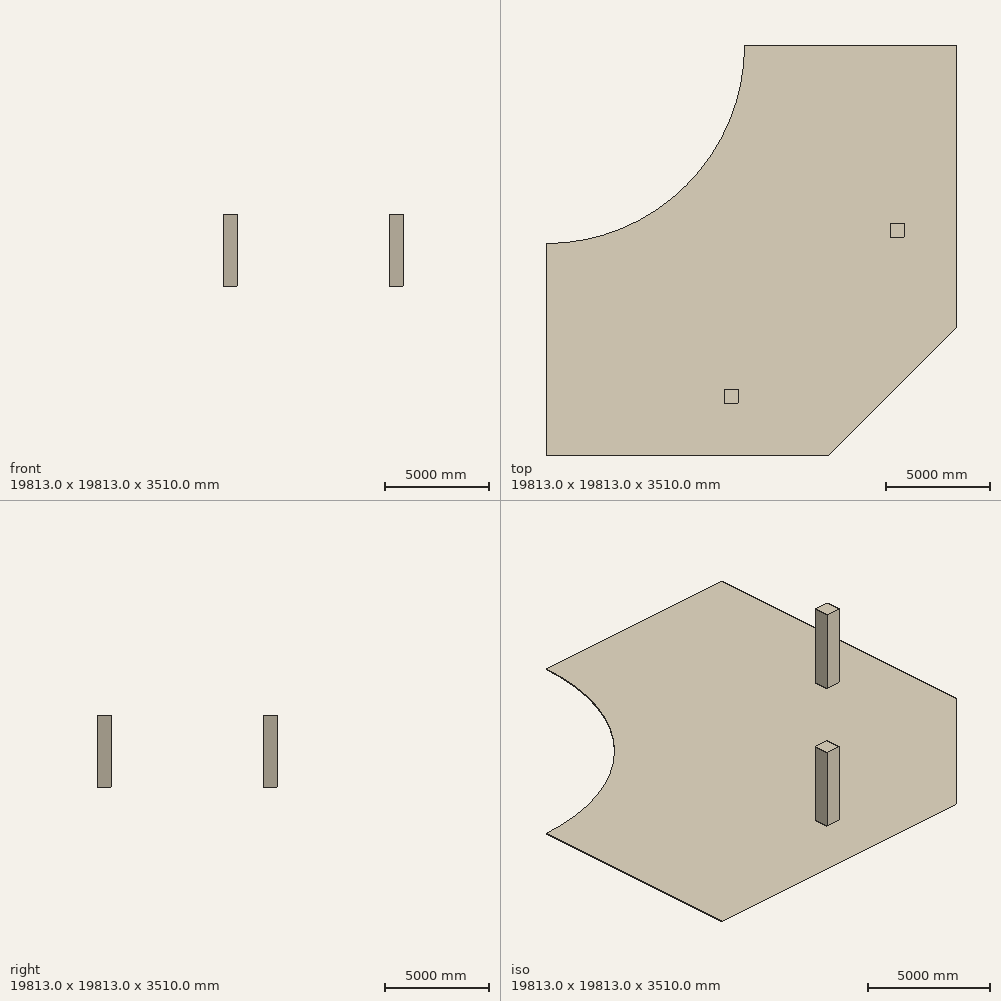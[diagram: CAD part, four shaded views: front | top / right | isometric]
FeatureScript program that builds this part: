
annotation { "Feature Type Name" : "Feature", "Feature Type Description" : "" }
export const myFeature = defineFeature(function(context is Context, id is Id, definition is map)
    precondition{}
    {
        {
            var Q0;
            Q0=qCreatedBy(makeId("Top.planeOp"),FACE);
            var sketch = newSketch(context, id + "F0", { "sketchPlane" : qUnion([Q0])});
            skLineSegment(sketch, "E0.bottom", {"start": v(0, 0) * mm, "end": v(13640, 0) * mm});
            skLineSegment(sketch, "E0.top", {"start": v(9573.04, 19813.04) * mm, "end": v(19813.04, 19813.04) * mm});
            skLineSegment(sketch, "E0.left", {"start": v(0, 0) * mm, "end": v(0, 10240) * mm});
            skLineSegment(sketch, "E0.right", {"start": v(19813.04, 6173.04) * mm, "end": v(19813.04, 19813.04) * mm});
            skLineSegment(sketch, "E1", {"start": v(13640, 0) * mm, "end": v(19813.04, 6173.04) * mm});
            skArc(sketch, "E2", {"start": v(0, 10240) * mm, "mid": v(6769.16, 13043.88) * mm, "end": v(9573.04, 19813.04) * mm});
            skLineSegment(sketch, "E3", {"start": v(19813.04, 10240) * mm, "end": v(0, 10240) * mm, "construction": true});
            skLineSegment(sketch, "E4", {"start": v(9573.04, 19813.04) * mm, "end": v(9573.04, 0) * mm, "construction": true});
            skLineSegment(sketch, "E5.bottom", {"start": v(16613.04, 11213.04) * mm, "end": v(17313.04, 11213.04) * mm});
            skLineSegment(sketch, "E5.top", {"start": v(16613.04, 10513.04) * mm, "end": v(17313.04, 10513.04) * mm});
            skLineSegment(sketch, "E5.left", {"start": v(16613.04, 11213.04) * mm, "end": v(16613.04, 10513.04) * mm});
            skLineSegment(sketch, "E5.right", {"start": v(17313.04, 11213.04) * mm, "end": v(17313.04, 10513.04) * mm});
            skLineSegment(sketch, "E6.bottom", {"start": v(8600, 3200) * mm, "end": v(9300, 3200) * mm});
            skLineSegment(sketch, "E6.top", {"start": v(8600, 2500) * mm, "end": v(9300, 2500) * mm});
            skLineSegment(sketch, "E6.left", {"start": v(8600, 3200) * mm, "end": v(8600, 2500) * mm});
            skLineSegment(sketch, "E6.right", {"start": v(9300, 3200) * mm, "end": v(9300, 2500) * mm});
            skSolve(sketch);
        }
        {
            var Q0;
            Q0=qCreatedBy(makeId("Top.planeOp"),FACE);
            var sketch = newSketch(context, id + "F1", { "sketchPlane" : qUnion([Q0])});
            skArc(sketch, "E7.0", {"start": v(0, 10240) * mm, "mid": v(6769.16, 13043.88) * mm, "end": v(9573.04, 19813.04) * mm});
            skLineSegment(sketch, "E7.1", {"start": v(0, 0) * mm, "end": v(0, 10240) * mm});
            skLineSegment(sketch, "E7.2", {"start": v(0, 0) * mm, "end": v(13640, 0) * mm});
            skLineSegment(sketch, "E7.3", {"start": v(13640, 0) * mm, "end": v(19813.04, 6173.04) * mm});
            skLineSegment(sketch, "E7.4", {"start": v(19813.04, 6173.04) * mm, "end": v(19813.04, 19813.04) * mm});
            skLineSegment(sketch, "E7.5", {"start": v(9573.04, 19813.04) * mm, "end": v(19813.04, 19813.04) * mm});
            skLineSegment(sketch, "E8.bottom", {"start": v(10187.24, 19813.04) * mm, "end": v(13187.24, 19813.04) * mm});
            skLineSegment(sketch, "E8.top", {"start": v(10187.24, 17813.04) * mm, "end": v(13187.24, 17813.04) * mm});
            skLineSegment(sketch, "E8.left", {"start": v(10187.24, 19813.04) * mm, "end": v(10187.24, 17813.04) * mm});
            skLineSegment(sketch, "E8.right", {"start": v(13187.24, 19813.04) * mm, "end": v(13187.24, 17813.04) * mm});
            skLineSegment(sketch, "E9.bottom", {"start": v(13187.24, 17813.04) * mm, "end": v(16187.24, 17813.04) * mm});
            skLineSegment(sketch, "E9.top", {"start": v(13187.24, 19813.04) * mm, "end": v(16187.24, 19813.04) * mm});
            skLineSegment(sketch, "E9.left", {"start": v(13187.24, 17813.04) * mm, "end": v(13187.24, 19813.04) * mm});
            skLineSegment(sketch, "E9.right", {"start": v(16187.24, 17813.04) * mm, "end": v(16187.24, 19813.04) * mm});
            skLineSegment(sketch, "E10.bottom", {"start": v(16187.24, 19813.04) * mm, "end": v(19187.24, 19813.04) * mm});
            skLineSegment(sketch, "E10.top", {"start": v(16187.24, 17813.04) * mm, "end": v(19187.24, 17813.04) * mm});
            skLineSegment(sketch, "E10.left", {"start": v(16187.24, 19813.04) * mm, "end": v(16187.24, 17813.04) * mm});
            skLineSegment(sketch, "E10.right", {"start": v(19187.24, 19813.04) * mm, "end": v(19187.24, 17813.04) * mm});
            skLineSegment(sketch, "E11.bottom", {"start": v(0, 9608.05) * mm, "end": v(2000, 9608.05) * mm});
            skLineSegment(sketch, "E11.top", {"start": v(0, 6608.05) * mm, "end": v(2000, 6608.05) * mm});
            skLineSegment(sketch, "E11.left", {"start": v(0, 9608.05) * mm, "end": v(0, 6608.05) * mm});
            skLineSegment(sketch, "E11.right", {"start": v(2000, 9608.05) * mm, "end": v(2000, 6608.05) * mm});
            skLineSegment(sketch, "E12.bottom", {"start": v(2000, 6608.05) * mm, "end": v(0, 6608.05) * mm});
            skLineSegment(sketch, "E12.top", {"start": v(2000, 3608.05) * mm, "end": v(0, 3608.05) * mm});
            skLineSegment(sketch, "E12.left", {"start": v(2000, 6608.05) * mm, "end": v(2000, 3608.05) * mm});
            skLineSegment(sketch, "E12.right", {"start": v(0, 6608.05) * mm, "end": v(0, 3608.05) * mm});
            skLineSegment(sketch, "E13.top", {"start": v(2000, 608.05) * mm, "end": v(0, 608.05) * mm});
            skLineSegment(sketch, "E13.left", {"start": v(2000, 3608.05) * mm, "end": v(2000, 608.05) * mm});
            skLineSegment(sketch, "E13.right", {"start": v(0, 3608.05) * mm, "end": v(0, 608.05) * mm});
            skLineSegment(sketch, "E14.bottom", {"start": v(4102.55, 608.05) * mm, "end": v(8102.55, 608.05) * mm});
            skLineSegment(sketch, "E14.top", {"start": v(4102.55, 6608.05) * mm, "end": v(8102.55, 6608.05) * mm});
            skLineSegment(sketch, "E14.left", {"start": v(4102.55, 608.05) * mm, "end": v(4102.55, 6608.05) * mm});
            skLineSegment(sketch, "E14.right", {"start": v(8102.55, 608.05) * mm, "end": v(8102.55, 6608.05) * mm});
            skLineSegment(sketch, "E15", {"start": v(6102.55, 6608.05) * mm, "end": v(6102.55, 608.05) * mm});
            skLineSegment(sketch, "E16", {"start": v(4102.55, 3608.05) * mm, "end": v(8102.55, 3608.05) * mm});
            skLineSegment(sketch, "E17.bottom", {"start": v(10033.35, 16637.1) * mm, "end": v(16033.35, 16637.1) * mm});
            skLineSegment(sketch, "E17.top", {"start": v(10033.35, 11637.1) * mm, "end": v(16033.35, 11637.1) * mm});
            skLineSegment(sketch, "E17.left", {"start": v(10033.35, 16637.1) * mm, "end": v(10033.35, 11637.1) * mm});
            skLineSegment(sketch, "E17.right", {"start": v(16033.35, 16637.1) * mm, "end": v(16033.35, 11637.1) * mm});
            skSolve(sketch);
        }
        {
            var Q0;
            Q0=qCreatedBy(makeId("Top.planeOp"),FACE);
            var sketch = newSketch(context, id + "F2", { "sketchPlane" : qUnion([Q0])});
            skArc(sketch, "E18.0", {"start": v(0, 10240) * mm, "mid": v(6769.16, 13043.88) * mm, "end": v(9573.04, 19813.04) * mm});
            skLineSegment(sketch, "E18.1", {"start": v(9573.04, 19813.04) * mm, "end": v(19813.04, 19813.04) * mm});
            skLineSegment(sketch, "E18.2", {"start": v(19813.04, 6173.04) * mm, "end": v(19813.04, 19813.04) * mm});
            skLineSegment(sketch, "E18.3", {"start": v(13640, 0) * mm, "end": v(19813.04, 6173.04) * mm});
            skLineSegment(sketch, "E18.4", {"start": v(0, 0) * mm, "end": v(13640, 0) * mm});
            skLineSegment(sketch, "E18.5", {"start": v(0, 0) * mm, "end": v(0, 10240) * mm});
            skSolve(sketch);
        }
        {
            var Q0;
            Q0 = qSketchRegion(id + "F2", true);
            extrude(context, id + "F3", {"entities" : qUnion([Q0]), "oppositeDirection" : true, "depth" : 10 * mm, "offsetDistance" : 25 * mm});
        }
        {
            var Q0;
            Q0=makeQuery(id+"F0.imprint","IMPRINT",FACE,{"disambiguationData":[TD([[makeQuery(id+"F0.imprint","IMPRINT",EDGE,{"derivedFrom":sQuery(id+"F0.wireOp",EDGE,"E6.bottom")}),-1.0]])]});
            var Q1;
            Q1=makeQuery(id+"F0.imprint","IMPRINT",FACE,{"disambiguationData":[TD([[makeQuery(id+"F0.imprint","IMPRINT",EDGE,{"derivedFrom":sQuery(id+"F0.wireOp",EDGE,"E5.bottom")}),-1.0]])]});
            extrude(context, id + "F4", {"entities" : qUnion([Q0, Q1]), "depth" : 3500 * mm, "offsetDistance" : 25 * mm});
        }
    });
